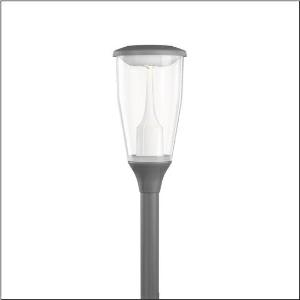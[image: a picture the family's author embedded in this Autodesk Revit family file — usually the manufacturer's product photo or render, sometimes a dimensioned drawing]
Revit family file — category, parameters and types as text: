
# Revit family: dl_11_iq___p1_0a_5xa5575ff14hp00022_3c96
name_source: partatom
category: Lighting Fixtures
units: mm (PartAtom-declared; Revit-internal decimal feet)

## family parameters
Cut with Voids When Loaded = No
Host = Face
Light Source = No
Part Type = Normal
Room Calculation Point = No
Round Connector Dimension = Use Diameter
Shared = No

## types (1)
- --- (1 x LED, 4780 lm, 33.6 W, 3000K)
    Apparent Load = 34 VA
    CIE Flux Codes = 23 60 93 95 100
    Color Rendering = 70
    Color Temperature = 3000K
    Default Elevation = 1800 mm
    Description = DL 11 iQ, mast luminaire, Module 540 iQ-SR, primary light control with 3 zone facetted reflector, of plastic, silver coated, highly specular, structured, primary optical cover: cover, of PMMA, transparent, light distribution: P1.0a, light emission: direct distribution, primary light characteristic: asymmetric, installation type: post-top, LED, High Power LED, light colour: 730, colour temperature: 3000K, control: Street-Remote, Auto-Match, Temp-Guard, Lumen-Switch, Night-Set, Smart-Wire, Light-Fading, Desk-Remote (wireless, voltage-free reading and setting of iQ features in the workshop via application-optimized NFC function/RFID function), optimised constant luminous flux control (CLO 2.0), mains connection: 220..240V, AC, 50/60Hz, connection cable pre-assembled, cable length: 5,5m, wiring characteristics: H07RN-F, 5-core, 1.5mm², start of lifetime: 34W, end of service life: 36W, luminaire housing, upper part, of diecast aluminium, coated, Siteco® metallic grey (DB 702S), spigot size: 76mm (post-top), post-top mast mounting element, of diecast aluminium, coated, Siteco® metallic grey (DB 702S), Module 540 iQ-SR, traffic white (RAL 9016), equipment: Power, protection rating (complete): IP66, insulation class (complete): insulation class II (safety insulation), certification: CE, ENEC, ENEC+, VDE, packaging unit: 1 piece

Light Distribution: P1.0a
    Height = 665 mm
    Lamp = 1 x LED
    Lamp Light Flux = 4780 lm
    Lamp Power = 33.6 W
    Lamp count = 1
    Length = 334 mm
    Luminous efficacy = 142 lm/W
    Manufacturer = Siteco
    ModVariant = No
    Model = 5XA5575FF14HP00022
    Number of Poles = 1
    OnlyDefault = Yes
    Power Factor = 1
    Product Name = DL 11 iQ | P1.0a
    Product group = mast luminaire | pylon top
    ProductGroupID = 6100
    Protection Class = Protection class II
    Protection Degree = IP 66
    RLX_Detail_Level = 1
    RLX_Emergency_Light_Flux = 0 lm
    RLX_Emergency_Type = 0
    RLX_Emergency_Type_DB = No
    RlxData = <blob elided: 103029 chars, md5=cf940e81>
    Socket = socket
    Standby Power = 0 W
    System Light Flux = 4780 lm
    System Power = 34 W
    Type Comments = factory setting: luminous flux: 100 % | dim-lin: 254 | 695 mA
    Type Image = l_1258354.jpg
    URL = http://relux.com
    VarID = @adj_021821
    Voltage = 0 V
    Weight = 0.00 kg
    Width = 0 mm  [stored 0 ft]

note: [stored X ft] marks values corroborated as IEEE doubles in the binary element streams (Revit-internal decimal feet)

## geometry (parser evidence)
native form markers: Blend x4, Sweep x11
no freeform markers — native parametric forms only
